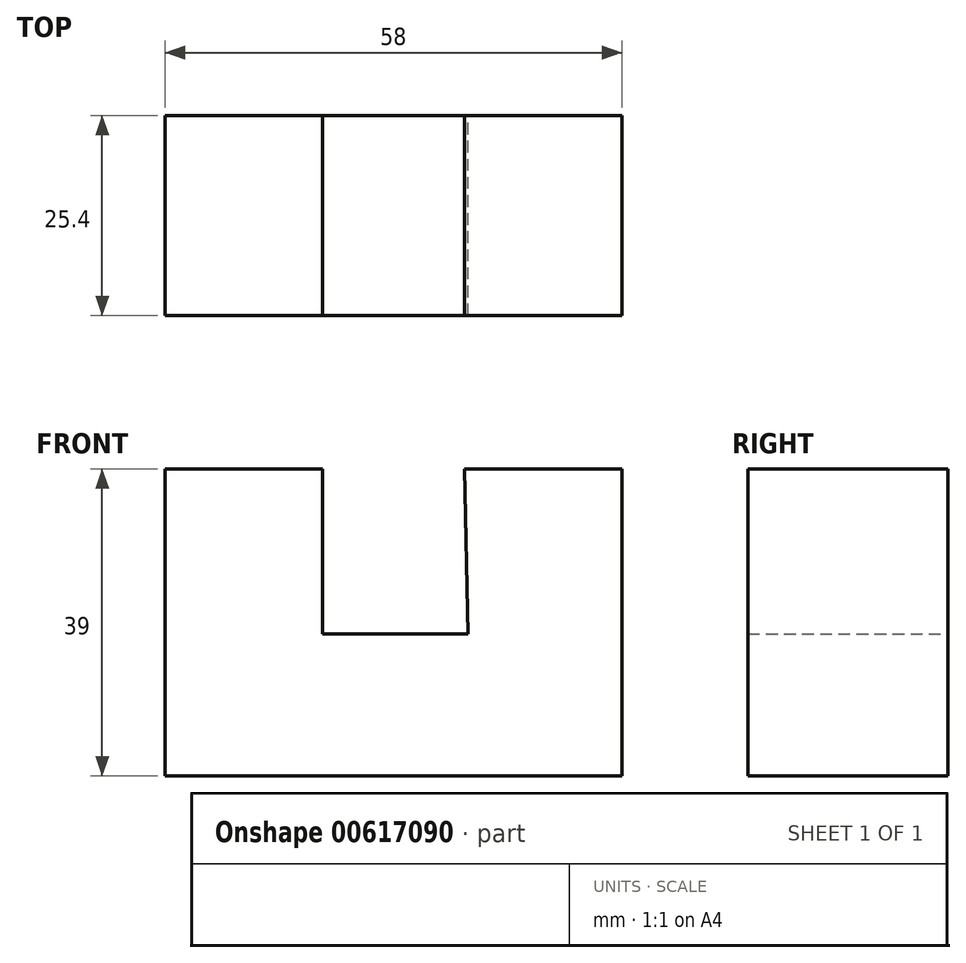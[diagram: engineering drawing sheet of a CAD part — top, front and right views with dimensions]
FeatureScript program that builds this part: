
annotation { "Feature Type Name" : "Feature", "Feature Type Description" : "" }
export const myFeature = defineFeature(function(context is Context, id is Id, definition is map)
    precondition{}
    {
        {
            var Q0;
            Q0=qCreatedBy(makeId("Front.planeOp"),FACE);
            var sketch = newSketch(context, id + "F0", { "sketchPlane" : qUnion([Q0])});
            skLineSegment(sketch, "E0", {"start": v(-27.64, 20.93) * mm, "end": v(-27.64, -18.07) * mm});
            skLineSegment(sketch, "E1", {"start": v(-27.64, -18.07) * mm, "end": v(30.36, -18.07) * mm});
            skLineSegment(sketch, "E2", {"start": v(30.36, -18.07) * mm, "end": v(30.36, 20.93) * mm});
            skLineSegment(sketch, "E3", {"start": v(30.36, 20.93) * mm, "end": v(10.36, 20.93) * mm});
            skLineSegment(sketch, "E4", {"start": v(10.82, 0) * mm, "end": v(-7.64, 0) * mm});
            skLineSegment(sketch, "E5", {"start": v(-7.64, 0) * mm, "end": v(-7.64, 20.93) * mm});
            skLineSegment(sketch, "E6", {"start": v(-7.64, 20.93) * mm, "end": v(-27.64, 20.93) * mm});
            skLineSegment(sketch, "E7", {"start": v(10.82, 0) * mm, "end": v(10.36, 20.93) * mm});
            skSolve(sketch);
        }
        {
            var Q0;
            Q0 = qSketchRegion(id + "F0", true);
            extrude(context, id + "F1", {"entities" : qUnion([Q0]), "depth" : 25.4 * mm, "offsetDistance" : 25.4 * mm});
        }
    });
